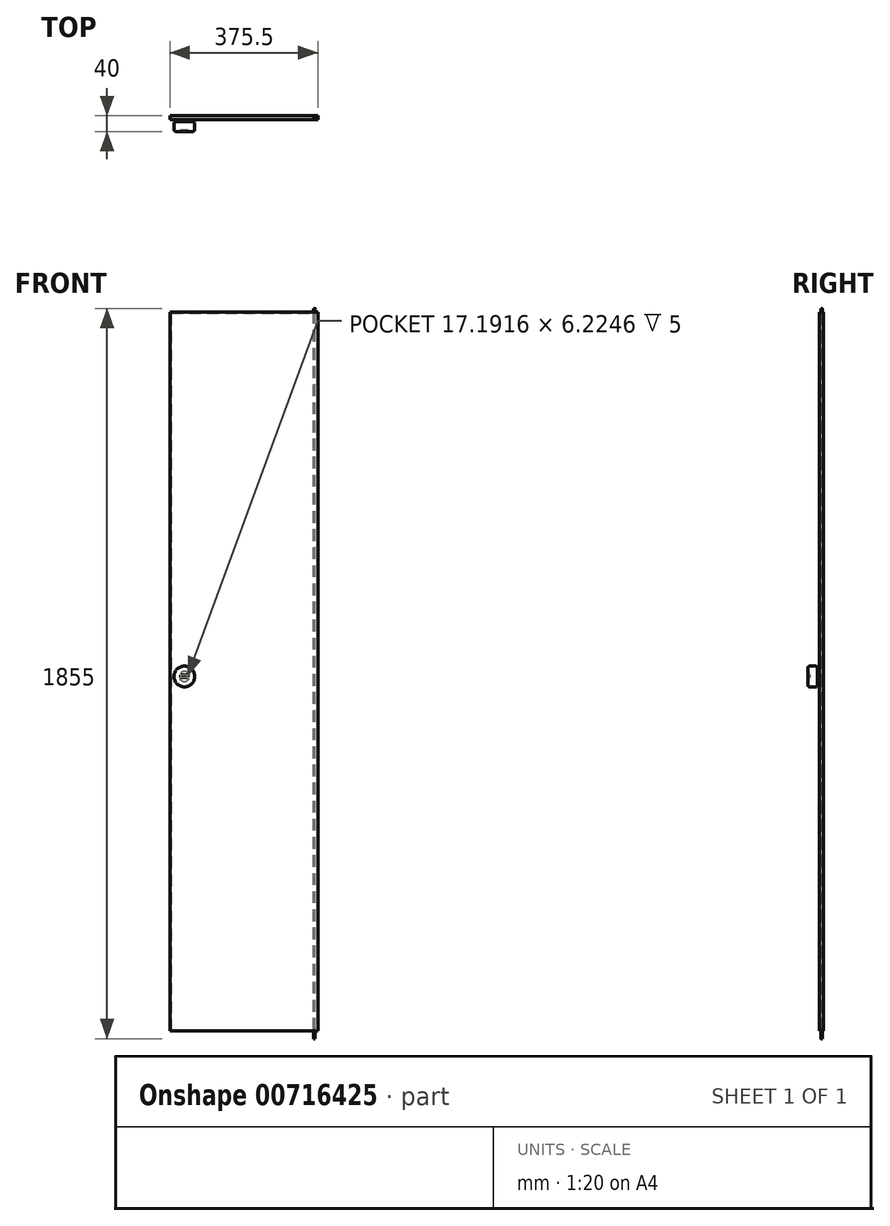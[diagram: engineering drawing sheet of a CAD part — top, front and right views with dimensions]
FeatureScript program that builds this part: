
annotation { "Feature Type Name" : "Feature", "Feature Type Description" : "" }
export const myFeature = defineFeature(function(context is Context, id is Id, definition is map)
    precondition{}
    {
        {
            var Q0;
            Q0=qCreatedBy(makeId("Top.planeOp"),FACE);
            var sketch = newSketch(context, id + "F0", { "sketchPlane" : qUnion([Q0])});
            skLineSegment(sketch, "E0.bottom", {"start": v(0, 0) * mm, "end": v(375.5, 0) * mm});
            skLineSegment(sketch, "E0.top", {"start": v(0, 10) * mm, "end": v(375.5, 10) * mm});
            skLineSegment(sketch, "E0.left", {"start": v(0, 0) * mm, "end": v(0, 10) * mm});
            skLineSegment(sketch, "E0.right", {"start": v(375.5, 0) * mm, "end": v(375.5, 10) * mm});
            skSolve(sketch);
        }
        {
            var Q0;
            Q0 = qSketchRegion(id + "F0", true);
            extrude(context, id + "F1", {"entities" : qUnion([Q0]), "depth" : 1825.5 * mm, "offsetDistance" : 25 * mm});
        }
        {
            var Q0;
            Q0=makeQuery(id+"F1.opExtrude","SWEPT_FACE",FACE,{"disambiguationData":[OSD([sQuery(id+"F0.wireOp",EDGE,"E0.top")])]});
            shell(context, id + "F2", {"entities" : qUnion([Q0]), "thickness" : 2.5 * mm});
        }
        {
            var Q0;
            Q0=makeQuery(id+"F1.opExtrude","CAP_FACE",FACE,{"disambiguationData":[OSD([sQuery(id+"F0.wireOp",EDGE,"E0.bottom"),sQuery(id+"F0.wireOp",EDGE,"E0.top"),sQuery(id+"F0.wireOp",EDGE,"E0.left"),sQuery(id+"F0.wireOp",EDGE,"E0.right")])],"isStart":true});
            var sketch = newSketch(context, id + "F3", { "sketchPlane" : qUnion([Q0])});
            skCircle(sketch, "E1", {"center": v(366.5, -5) * mm, "radius": 2 * mm});
            skPoint(sketch, "E1.centerSnap0", {"position": v(375.5, -5) * mm});
            skSolve(sketch);
        }
        {
            var Q0;
            Q0 = qSketchRegion(id + "F3", true);
            extrude(context, id + "F4", {"entities" : qUnion([Q0]), "operationType" : NewBodyOperationType.ADD, "depth" : 20 * mm, "offsetDistance" : 25 * mm, "hasSecondDirection" : true, "secondDirectionOppositeDirection" : true, "secondDirectionDepth" : 1835 * mm});
        }
        {
            var Q0;
            Q0=makeQuery(id+"F1.opExtrude","SWEPT_FACE",FACE,{"disambiguationData":[OSD([sQuery(id+"F0.wireOp",EDGE,"E0.bottom")])]});
            var sketch = newSketch(context, id + "F5", { "sketchPlane" : qUnion([Q0])});
            skCircle(sketch, "E2", {"center": v(36.47, 900.13) * mm, "radius": 12.88 * mm});
            skSolve(sketch);
        }
        {
            var Q0;
            Q0 = qSketchRegion(id + "F5", true);
            extrude(context, id + "F6", {"entities" : qUnion([Q0]), "operationType" : NewBodyOperationType.ADD, "depth" : 5 * mm, "offsetDistance" : 25 * mm});
        }
        {
            var Q0;
            Q0=makeQuery(id+"F6.opExtrude","CAP_FACE",FACE,{"disambiguationData":[OSD([sQuery(id+"F5.wireOp",EDGE,"E2")])],"isStart":false});
            var sketch = newSketch(context, id + "F7", { "sketchPlane" : qUnion([Q0])});
            skCircle(sketch, "E3", {"center": v(36.47, 900.13) * mm, "radius": 26.34 * mm});
            skSolve(sketch);
        }
        {
            var Q0;
            Q0 = qSketchRegion(id + "F7", true);
            extrude(context, id + "F8", {"entities" : qUnion([Q0]), "operationType" : NewBodyOperationType.ADD, "depth" : 25 * mm, "offsetDistance" : 25 * mm});
        }
        {
            var Q0;
            Q0=makeQuery(id+"F8.opExtrude","CAP_EDGE",EDGE,{"disambiguationData":[OSD([sQuery(id+"F7.wireOp",EDGE,"E3")])],"isStart":false});
            var Q1;
            Q1=makeQuery(id+"F8.opExtrude","CAP_EDGE",EDGE,{"disambiguationData":[OSD([sQuery(id+"F7.wireOp",EDGE,"E3")])],"isStart":true});
            fillet(context, id + "F9", {"entities" : qUnion([Q0, Q1]), "radius" : 5 * mm, "tangentPropagation" : true, "allowEdgeOverflow" : false});
        }
        {
            var Q0;
            Q0=makeQuery(id+"F8.opExtrude","CAP_FACE",FACE,{"disambiguationData":[OSD([sQuery(id+"F7.wireOp",EDGE,"E3")])],"isStart":false});
            var sketch = newSketch(context, id + "F10", { "sketchPlane" : qUnion([Q0])});
            skLineSegment(sketch, "E4.bottom", {"start": v(27.35, 903.6) * mm, "end": v(44.54, 903.6) * mm});
            skLineSegment(sketch, "E4.top", {"start": v(27.35, 897.38) * mm, "end": v(44.54, 897.38) * mm});
            skLineSegment(sketch, "E4.left", {"start": v(27.35, 903.6) * mm, "end": v(27.35, 897.38) * mm});
            skLineSegment(sketch, "E4.right", {"start": v(44.54, 903.6) * mm, "end": v(44.54, 897.38) * mm});
            skSolve(sketch);
        }
        {
            var Q0;
            Q0 = qSketchRegion(id + "F10", true);
            extrude(context, id + "F11", {"entities" : qUnion([Q0]), "operationType" : NewBodyOperationType.REMOVE, "oppositeDirection" : true, "depth" : 5 * mm, "offsetDistance" : 25 * mm});
        }
    });
